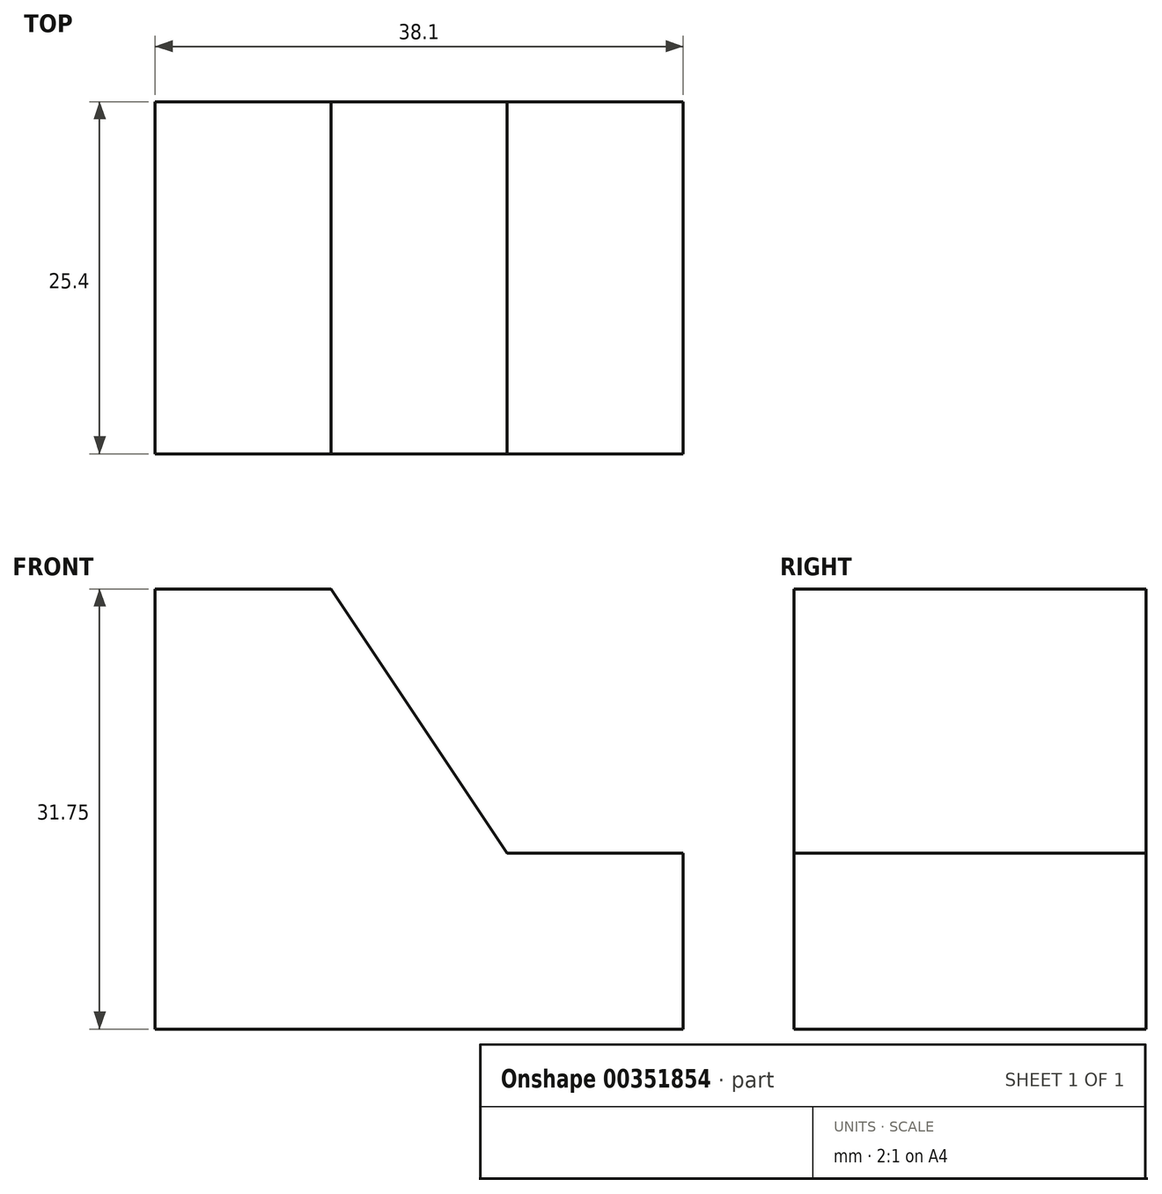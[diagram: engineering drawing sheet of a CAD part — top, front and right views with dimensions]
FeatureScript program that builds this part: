
annotation { "Feature Type Name" : "Feature", "Feature Type Description" : "" }
export const myFeature = defineFeature(function(context is Context, id is Id, definition is map)
    precondition{}
    {
        {
            var Q0;
            Q0=qCreatedBy(makeId("Front.planeOp"),FACE);
            var sketch = newSketch(context, id + "F0", { "sketchPlane" : qUnion([Q0])});
            skLineSegment(sketch, "E0", {"start": v(0, 0) * mm, "end": v(38.1, 0) * mm});
            skLineSegment(sketch, "E1", {"start": v(38.1, 0) * mm, "end": v(38.1, 12.7) * mm});
            skLineSegment(sketch, "E2", {"start": v(38.1, 12.7) * mm, "end": v(25.4, 12.7) * mm});
            skLineSegment(sketch, "E3", {"start": v(25.4, 12.7) * mm, "end": v(12.7, 31.75) * mm});
            skLineSegment(sketch, "E4", {"start": v(12.7, 31.75) * mm, "end": v(0, 31.75) * mm});
            skLineSegment(sketch, "E5", {"start": v(0, 31.75) * mm, "end": v(0, 0) * mm});
            skSolve(sketch);
        }
        {
            var Q0;
            Q0 = qSketchRegion(id + "F0", true);
            extrude(context, id + "F1", {"entities" : qUnion([Q0]), "depth" : 25.4 * mm});
        }
    });
